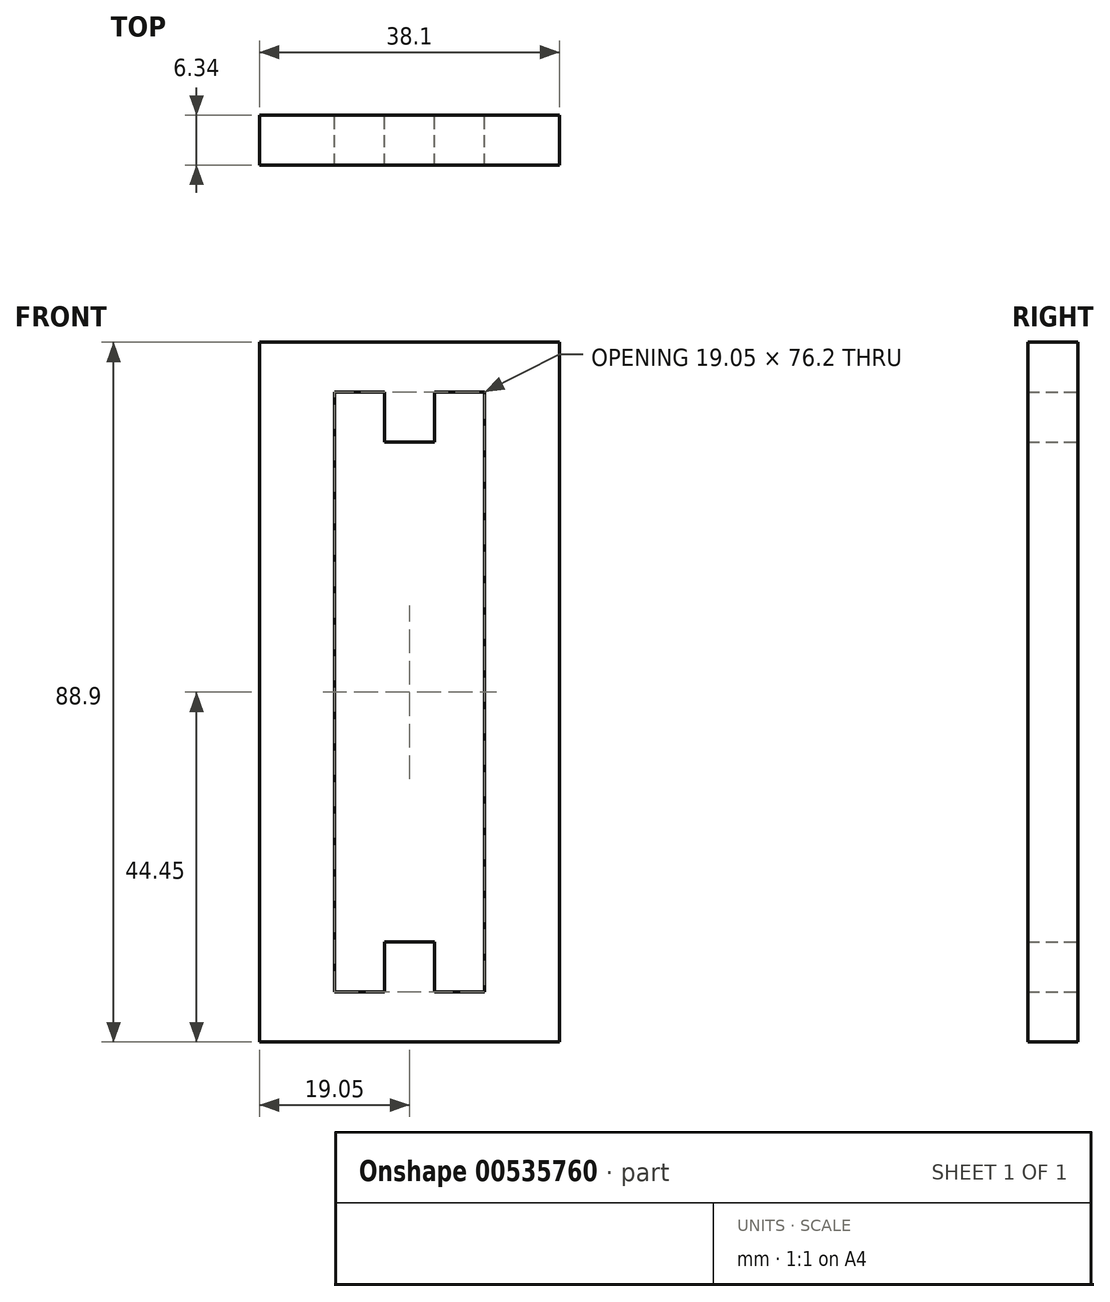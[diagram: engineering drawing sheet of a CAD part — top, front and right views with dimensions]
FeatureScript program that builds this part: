
annotation { "Feature Type Name" : "Feature", "Feature Type Description" : "" }
export const myFeature = defineFeature(function(context is Context, id is Id, definition is map)
    precondition{}
    {
        {
            var Q0;
            Q0=qCreatedBy(makeId("Front.planeOp"),FACE);
            var sketch = newSketch(context, id + "F0", { "sketchPlane" : qUnion([Q0])});
            skLineSegment(sketch, "E0.bottom", {"start": v(19.05, 44.45) * mm, "end": v(-19.05, 44.45) * mm});
            skLineSegment(sketch, "E0.top", {"start": v(19.05, -44.45) * mm, "end": v(-19.05, -44.45) * mm});
            skLineSegment(sketch, "E0.left", {"start": v(19.05, 44.45) * mm, "end": v(19.05, -44.45) * mm});
            skLineSegment(sketch, "E0.right", {"start": v(-19.05, 44.45) * mm, "end": v(-19.05, -44.45) * mm});
            skPoint(sketch, "E0.middle", {"position": v(0, 0) * mm});
            skLineSegment(sketch, "E1", {"start": v(-3.17, 38.1) * mm, "end": v(-3.17, 31.75) * mm});
            skLineSegment(sketch, "E2", {"start": v(-3.17, 31.75) * mm, "end": v(3.18, 31.75) * mm});
            skLineSegment(sketch, "E3", {"start": v(3.18, 31.75) * mm, "end": v(3.18, 38.1) * mm});
            skLineSegment(sketch, "E4", {"start": v(-3.17, 38.1) * mm, "end": v(-9.52, 38.1) * mm});
            skLineSegment(sketch, "E5", {"start": v(-9.52, 38.1) * mm, "end": v(-9.53, -38.1) * mm});
            skLineSegment(sketch, "E6.MirrorCS", {"start": v(9.53, 38.1) * mm, "end": v(9.53, -38.1) * mm});
            skLineSegment(sketch, "E7.MirrorCS", {"start": v(3.17, 38.1) * mm, "end": v(9.52, 38.1) * mm});
            skLineSegment(sketch, "E8.MirrorCS", {"start": v(-3.17, -38.1) * mm, "end": v(-3.17, -31.75) * mm});
            skLineSegment(sketch, "E9.MirrorCS", {"start": v(-3.17, -31.75) * mm, "end": v(3.18, -31.75) * mm});
            skLineSegment(sketch, "E10.MirrorCS", {"start": v(3.18, -31.75) * mm, "end": v(3.18, -38.1) * mm});
            skLineSegment(sketch, "E11.MirrorCS", {"start": v(3.17, -38.1) * mm, "end": v(9.52, -38.1) * mm});
            skLineSegment(sketch, "E12.MirrorCS", {"start": v(-3.17, -38.1) * mm, "end": v(-9.52, -38.1) * mm});
            skPoint(sketch, "E13.orphan", {"position": v(-3.17, 44.45) * mm});
            skPoint(sketch, "E14.orphan", {"position": v(3.18, 44.45) * mm});
            skPoint(sketch, "E15.orphan", {"position": v(3.18, -44.45) * mm});
            skPoint(sketch, "E16.orphan", {"position": v(-3.17, -44.45) * mm});
            skSolve(sketch);
        }
        {
            var Q0;
            Q0=makeQuery(id+"F0.imprint","IMPRINT",FACE,{"disambiguationData":[TD([[makeQuery(id+"F0.imprint","IMPRINT",EDGE,{"derivedFrom":sQuery(id+"F0.wireOp",EDGE,"E0.bottom")}),1.0]])]});
            extrude(context, id + "F1", {"entities" : qUnion([Q0]), "endBound" : BoundingType.SYMMETRIC, "depth" : 6.35 * mm, "offsetDistance" : 25.4 * mm});
        }
    });
